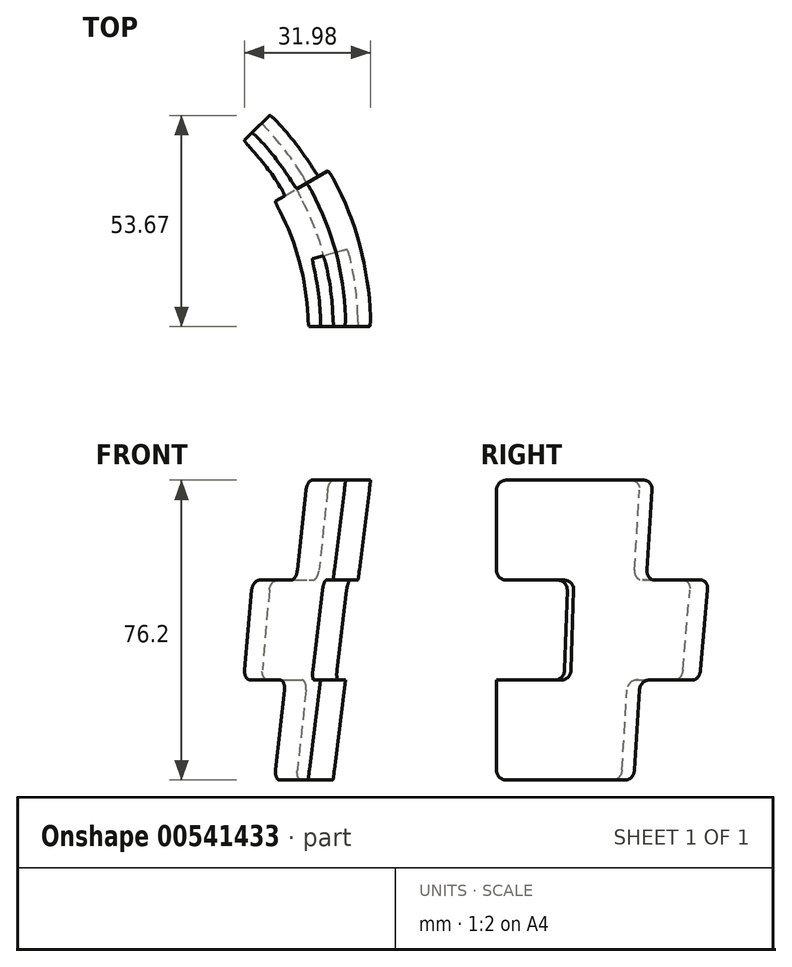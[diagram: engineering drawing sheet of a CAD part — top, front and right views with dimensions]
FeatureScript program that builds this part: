
annotation { "Feature Type Name" : "Feature", "Feature Type Description" : "" }
export const myFeature = defineFeature(function(context is Context, id is Id, definition is map)
    precondition{}
    {
        {
            var Q0;
            Q0=qCreatedBy(makeId("Front.planeOp"),FACE);
            var sketch = newSketch(context, id + "F0", { "sketchPlane" : qUnion([Q0])});
            skLineSegment(sketch, "E0", {"start": v(0, 0) * mm, "end": v(69.85, 0) * mm});
            skLineSegment(sketch, "E1", {"start": v(0, 0) * mm, "end": v(0, 76.2) * mm});
            skLineSegment(sketch, "E2", {"start": v(0, 76.2) * mm, "end": v(79.38, 76.2) * mm});
            skLineSegment(sketch, "E3", {"start": v(79.37, 76.2) * mm, "end": v(69.85, 0) * mm});
            skLineSegment(sketch, "E4", {"start": v(0, 76.2) * mm, "end": v(0, 47) * mm, "construction": true});
            skLineSegment(sketch, "E5", {"start": v(0, 76.2) * mm, "end": v(0, 50.8) * mm, "construction": true});
            skLineSegment(sketch, "E6", {"start": v(0, 50.8) * mm, "end": v(0, 25.4) * mm, "construction": true});
            skLineSegment(sketch, "E7", {"start": v(0, 25.4) * mm, "end": v(0, 0) * mm, "construction": true});
            skLineSegment(sketch, "E8", {"start": v(0, 50.8) * mm, "end": v(76.2, 50.8) * mm, "construction": true});
            skLineSegment(sketch, "E9", {"start": v(0, 25.4) * mm, "end": v(73.03, 25.4) * mm, "construction": true});
            skSolve(sketch);
        }
        {
            var Q0;
            Q0=makeQuery(id+"F0.imprint","IMPRINT",FACE,{"disambiguationData":[TD([[makeQuery(id+"F0.imprint","IMPRINT",EDGE,{"derivedFrom":sQuery(id+"F0.wireOp",EDGE,"E0")}),1.0]])]});
            var Q1;
            Q1=sQuery(id+"F0.wireOp",EDGE,"E1");
            revolve(context, id + "F1", {"entities" : qUnion([Q0]), "axis" : qUnion([Q1]), "revolveType" : RevolveType.ONE_DIRECTION, "angle" : 30 * degree});
        }
        {
            var Q0;
            Q0=makeQuery(id+"F1.opRevolve","CAP_FACE",FACE,{"disambiguationData":[OSD([sQuery(id+"F0.wireOp",EDGE,"E0"),sQuery(id+"F0.wireOp",EDGE,"E1"),sQuery(id+"F0.wireOp",EDGE,"E2"),sQuery(id+"F0.wireOp",EDGE,"E3")])],"isStart":true});
            var sketch = newSketch(context, id + "F2", { "sketchPlane" : qUnion([Q0])});
            skLineSegment(sketch, "E10", {"start": v(0, 76.2) * mm, "end": v(0, 0) * mm});
            skLineSegment(sketch, "E11", {"start": v(0, 0) * mm, "end": v(63.5, 0) * mm});
            skLineSegment(sketch, "E12", {"start": v(0, 76.2) * mm, "end": v(73.03, 76.2) * mm});
            skLineSegment(sketch, "E13", {"start": v(73.03, 76.2) * mm, "end": v(63.5, 0) * mm});
            skSolve(sketch);
        }
        {
            var Q0;
            Q0=makeQuery(id+"F1.opRevolve","CAP_FACE",FACE,{"disambiguationData":[OSD([sQuery(id+"F0.wireOp",EDGE,"E0"),sQuery(id+"F0.wireOp",EDGE,"E1"),sQuery(id+"F0.wireOp",EDGE,"E2"),sQuery(id+"F0.wireOp",EDGE,"E3")])],"isStart":true});
            var sketch = newSketch(context, id + "F3", { "sketchPlane" : qUnion([Q0])});
            skLineSegment(sketch, "E14", {"start": v(0, 0) * mm, "end": v(0, 76.2) * mm, "construction": true});
            skLineSegment(sketch, "E15", {"start": v(0, 76.2) * mm, "end": v(0, 50.8) * mm, "construction": true});
            skLineSegment(sketch, "E16", {"start": v(0, 50.8) * mm, "end": v(76.2, 50.8) * mm});
            skLineSegment(sketch, "E17", {"start": v(0, 50.8) * mm, "end": v(0, 25.4) * mm});
            skLineSegment(sketch, "E18", {"start": v(0, 25.4) * mm, "end": v(73.03, 25.4) * mm});
            skLineSegment(sketch, "E19", {"start": v(73.03, 25.4) * mm, "end": v(76.2, 50.8) * mm});
            skSolve(sketch);
        }
        {
            var Q0;
            Q0=qSketchRegion(id+"F3",true);
            var Q1;
            Q1=sQuery(id+"F3.wireOp",EDGE,"E17");
            revolve(context, id + "F4", {"operationType" : NewBodyOperationType.ADD, "entities" : qUnion([Q0]), "axis" : qUnion([Q1]), "revolveType" : RevolveType.ONE_DIRECTION, "oppositeDirection" : true, "angle" : 45 * degree});
        }
        {
            var Q0;
            Q0=qSketchRegion(id+"F3",true);
            var Q1;
            Q1=sQuery(id+"F3.wireOp",EDGE,"E17");
            revolve(context, id + "F5", {"operationType" : NewBodyOperationType.REMOVE, "entities" : qUnion([Q0]), "axis" : qUnion([Q1]), "revolveType" : RevolveType.ONE_DIRECTION, "oppositeDirection" : true, "angle" : 15 * degree});
        }
        {
            var Q0;
            Q0=makeQuery(id+"F2.imprint","IMPRINT",FACE,{"disambiguationData":[TD([[makeQuery(id+"F2.imprint","IMPRINT",EDGE,{"derivedFrom":sQuery(id+"F2.wireOp",EDGE,"E10")}),-1.0]])]});
            var Q1;
            Q1=sQuery(id+"F2.wireOp",EDGE,"E10");
            revolve(context, id + "F6", {"operationType" : NewBodyOperationType.REMOVE, "entities" : qUnion([Q0]), "axis" : qUnion([Q1]), "revolveType" : RevolveType.FULL, "oppositeDirection" : true});
        }
        {
            var Q0;
            Q0=makeQuery(id+"F1.opRevolve","CAP_EDGE",EDGE,{"disambiguationData":[OSD([sQuery(id+"F0.wireOp",EDGE,"E0")])],"isStart":false});
            var Q1;
            Q1=makeQuery(id+"F1.opRevolve","CAP_EDGE",EDGE,{"disambiguationData":[OSD([sQuery(id+"F0.wireOp",EDGE,"E0")])],"isStart":true});
            var Q2;
            Q2=makeQuery(id+"F5.boolean.opBoolean","COPY",EDGE,{"derivedFrom":makeQuery(id+"F5.opRevolve","CAP_EDGE",EDGE,{"disambiguationData":[OSD([sQuery(id+"F3.wireOp",EDGE,"E18")])],"isStart":true})});
            var Q3;
            Q3=makeQuery(id+"F5.boolean.opBoolean","COPY",EDGE,{"derivedFrom":makeQuery(id+"F5.opRevolve","CAP_EDGE",EDGE,{"disambiguationData":[OSD([sQuery(id+"F3.wireOp",EDGE,"E18")])],"isStart":false})});
            var Q4;
            Q4=makeQuery(id+"F5.boolean.opBoolean","COPY",EDGE,{"derivedFrom":makeQuery(id+"F5.opRevolve","CAP_EDGE",EDGE,{"disambiguationData":[OSD([sQuery(id+"F3.wireOp",EDGE,"E16")])],"isStart":false})});
            var Q5;
            Q5=makeQuery(id+"F5.boolean.opBoolean","COPY",EDGE,{"derivedFrom":makeQuery(id+"F5.opRevolve","CAP_EDGE",EDGE,{"disambiguationData":[OSD([sQuery(id+"F3.wireOp",EDGE,"E16")])],"isStart":true})});
            var Q6;
            Q6=makeQuery(id+"F1.opRevolve","CAP_EDGE",EDGE,{"disambiguationData":[OSD([sQuery(id+"F0.wireOp",EDGE,"E2")])],"isStart":true});
            var Q7;
            Q7=makeQuery(id+"F1.opRevolve","CAP_EDGE",EDGE,{"disambiguationData":[OSD([sQuery(id+"F0.wireOp",EDGE,"E2")])],"isStart":false});
            var Q8;
            Q8=makeQuery(id+"F4.boolean.opBoolean","INTERSECT",EDGE,{"derivedFrom":[makeQuery(id+"F1.opRevolve","CAP_FACE",FACE,{"disambiguationData":[OSD([sQuery(id+"F0.wireOp",EDGE,"E0"),sQuery(id+"F0.wireOp",EDGE,"E1"),sQuery(id+"F0.wireOp",EDGE,"E2"),sQuery(id+"F0.wireOp",EDGE,"E3")])],"isStart":false}),makeQuery(id+"F4.opRevolve","SWEPT_FACE",FACE,{"disambiguationData":[OSD([sQuery(id+"F3.wireOp",EDGE,"E16")])]})]});
            var Q9;
            Q9=makeQuery(id+"F4.opRevolve","CAP_EDGE",EDGE,{"disambiguationData":[OSD([sQuery(id+"F3.wireOp",EDGE,"E16")])],"isStart":false});
            var Q10;
            Q10=makeQuery(id+"F4.opRevolve","CAP_EDGE",EDGE,{"disambiguationData":[OSD([sQuery(id+"F3.wireOp",EDGE,"E18")])],"isStart":false});
            var Q11;
            Q11=makeQuery(id+"F4.boolean.opBoolean","INTERSECT",EDGE,{"derivedFrom":[makeQuery(id+"F1.opRevolve","CAP_FACE",FACE,{"disambiguationData":[OSD([sQuery(id+"F0.wireOp",EDGE,"E0"),sQuery(id+"F0.wireOp",EDGE,"E1"),sQuery(id+"F0.wireOp",EDGE,"E2"),sQuery(id+"F0.wireOp",EDGE,"E3")])],"isStart":false}),makeQuery(id+"F4.opRevolve","SWEPT_FACE",FACE,{"disambiguationData":[OSD([sQuery(id+"F3.wireOp",EDGE,"E18")])]})]});
            fillet(context, id + "F7", {"entities" : qUnion([Q0, Q1, Q2, Q3, Q4, Q5, Q6, Q7, Q8, Q9, Q10, Q11]), "radius" : 2.54 * mm, "tangentPropagation" : true, "allowEdgeOverflow" : false});
        }
    });
